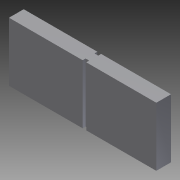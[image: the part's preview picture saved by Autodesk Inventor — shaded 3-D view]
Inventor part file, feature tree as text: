
AUTODESK INVENTOR PART (.ipt)
format: ipt  version: 2012 (Build 160160000, 160)  size: 87,552 bytes
history: native  units: in
note: dims shown in document units (in); Inventor stores cm internally (conversion verified against a paired STEP export)
features: extrude x3, sketch x3
ambient origin geometry x8: Origin, YZ Plane, XZ Plane, XY Plane, X Axis, Y Axis, Z Axis, Center Point
bodies: Solid1 (feature_tree)
feature tree (6):
  extrude  "Extrusion1"  Depth=2.0in
  extrude  "Extrusion2"  Depth=0.1in TaperAngle=0.0deg
  extrude  "Extrusion3"  [1 undecoded]
  sketch  "Sketch1"  dims[d0=5.0in d1=2.0in]
  sketch  "Sketch2"  dims[d2=0.5in d3=0.0in d4=0.1in d5=0.0in]
  sketch  "Sketch3"  dims[d6=0.1in d7=0.0in]
note: 1 required parameter value undecoded (feature->parameter linkage not recoverable at this tier; creation-order binding heuristic only, values carry confidence <= 0.55)
